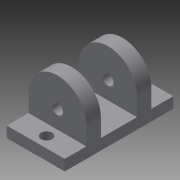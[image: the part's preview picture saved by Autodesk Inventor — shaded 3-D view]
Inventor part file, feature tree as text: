
AUTODESK INVENTOR PART (.ipt)
format: ipt  version: 2015 (Build 190159000, 159)  size: 134,144 bytes
history: native  units: in
note: dims shown in document units (in); Inventor stores cm internally (conversion verified against a paired STEP export)
features: extrude x5, sketch x3
ambient origin geometry x8: Origin, YZ Plane, XZ Plane, XY Plane, X Axis, Y Axis, Z Axis, Center Point
bodies: Solid1 (feature_tree)
feature tree (8):
  sketch  "Sketch1"  dims[d0=1.1811in d1=0.6299in]
  extrude  "Extrusion1"  Depth=0.6299in
  extrude  "Extrusion2"  Depth=0.1181in
  sketch  "Sketch2"  dims[d2=0.1181in d3=0.1181in]
  extrude  "Extrusion3"  Depth=1.1811in
  extrude  "Extrusion4"  Depth=0.1181in
  extrude  "Extrusion5"  Depth=0.1181in
  sketch  "Sketch3"  dims[d4=0.122in d5=0.122in d6=0.1181in d7=0.1181in d8=0.1575in d9=0.1575in d10=0.1181in d11=0.0in d12=0.1969in d13=0.0in d14=0.1181in d15=0.1575in d16=0.0in d17=0.1575in d18=0.0in d19=1.1811in d20=0.0in]
